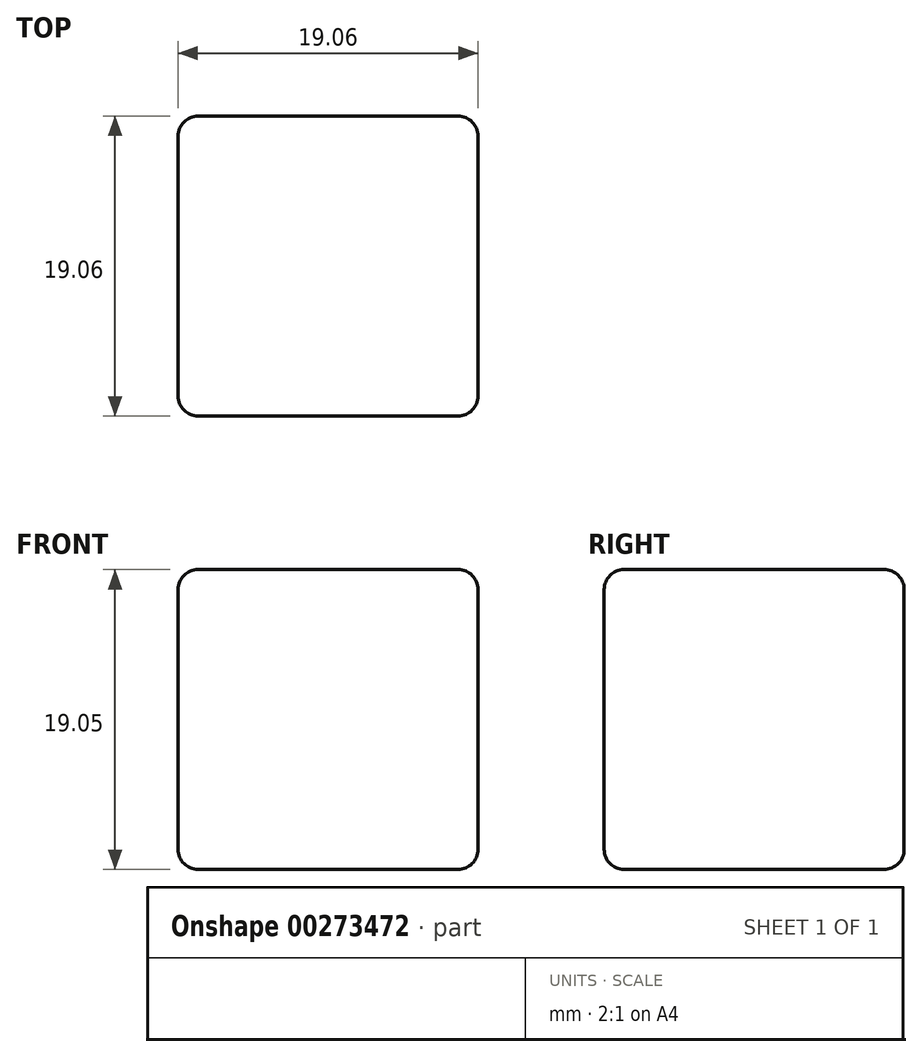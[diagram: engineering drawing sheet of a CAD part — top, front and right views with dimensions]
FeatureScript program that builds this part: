
annotation { "Feature Type Name" : "Feature", "Feature Type Description" : "" }
export const myFeature = defineFeature(function(context is Context, id is Id, definition is map)
    precondition{}
    {
        {
            var Q0;
            Q0=qCreatedBy(makeId("Top.planeOp"),FACE);
            var sketch = newSketch(context, id + "F0", { "sketchPlane" : qUnion([Q0])});
            skLineSegment(sketch, "E0.bottom", {"start": v(9.53, 9.52) * mm, "end": v(-9.53, 9.52) * mm});
            skLineSegment(sketch, "E0.top", {"start": v(9.53, -9.53) * mm, "end": v(-9.53, -9.53) * mm});
            skLineSegment(sketch, "E0.left", {"start": v(9.53, 9.52) * mm, "end": v(9.53, -9.53) * mm});
            skLineSegment(sketch, "E0.right", {"start": v(-9.53, 9.52) * mm, "end": v(-9.53, -9.53) * mm});
            skPoint(sketch, "E0.middle", {"position": v(0, 0) * mm});
            skSolve(sketch);
        }
        {
            var Q0;
            Q0 = qSketchRegion(id + "F0", true);
            var Q1;
            Q1=makeQuery(id+"F0.imprint","IMPRINT",FACE,{"disambiguationData":[TD([[makeQuery(id+"F0.imprint","IMPRINT",EDGE,{"derivedFrom":sQuery(id+"F0.wireOp",EDGE,"E0.bottom")}),1.0]])]});
            extrude(context, id + "F1", {"entities" : qUnion([Q0, Q1]), "depth" : 19.05 * mm});
        }
        {
            var Q0;
            Q0=makeQuery(id+"F1.opExtrude","CAP_FACE",FACE,{"disambiguationData":[OSD([sQuery(id+"F0.wireOp",EDGE,"E0.bottom"),sQuery(id+"F0.wireOp",EDGE,"E0.top"),sQuery(id+"F0.wireOp",EDGE,"E0.left"),sQuery(id+"F0.wireOp",EDGE,"E0.right")])],"isStart":false});
            var Q1;
            Q1=makeQuery(id+"F1.opExtrude","SWEPT_FACE",FACE,{"disambiguationData":[OSD([sQuery(id+"F0.wireOp",EDGE,"E0.left")])]});
            var Q2;
            Q2=makeQuery(id+"F1.opExtrude","SWEPT_FACE",FACE,{"disambiguationData":[OSD([sQuery(id+"F0.wireOp",EDGE,"E0.top")])]});
            var Q3;
            Q3=makeQuery(id+"F1.opExtrude","CAP_FACE",FACE,{"disambiguationData":[OSD([sQuery(id+"F0.wireOp",EDGE,"E0.bottom"),sQuery(id+"F0.wireOp",EDGE,"E0.top"),sQuery(id+"F0.wireOp",EDGE,"E0.left"),sQuery(id+"F0.wireOp",EDGE,"E0.right")])],"isStart":true});
            var Q4;
            Q4=makeQuery(id+"F1.opExtrude","SWEPT_FACE",FACE,{"disambiguationData":[OSD([sQuery(id+"F0.wireOp",EDGE,"E0.bottom")])]});
            fillet(context, id + "F2", {"entities" : qUnion([Q0, Q1, Q2, Q3, Q4]), "radius" : 1.27 * mm, "tangentPropagation" : true, "allowEdgeOverflow" : false});
        }
    });
